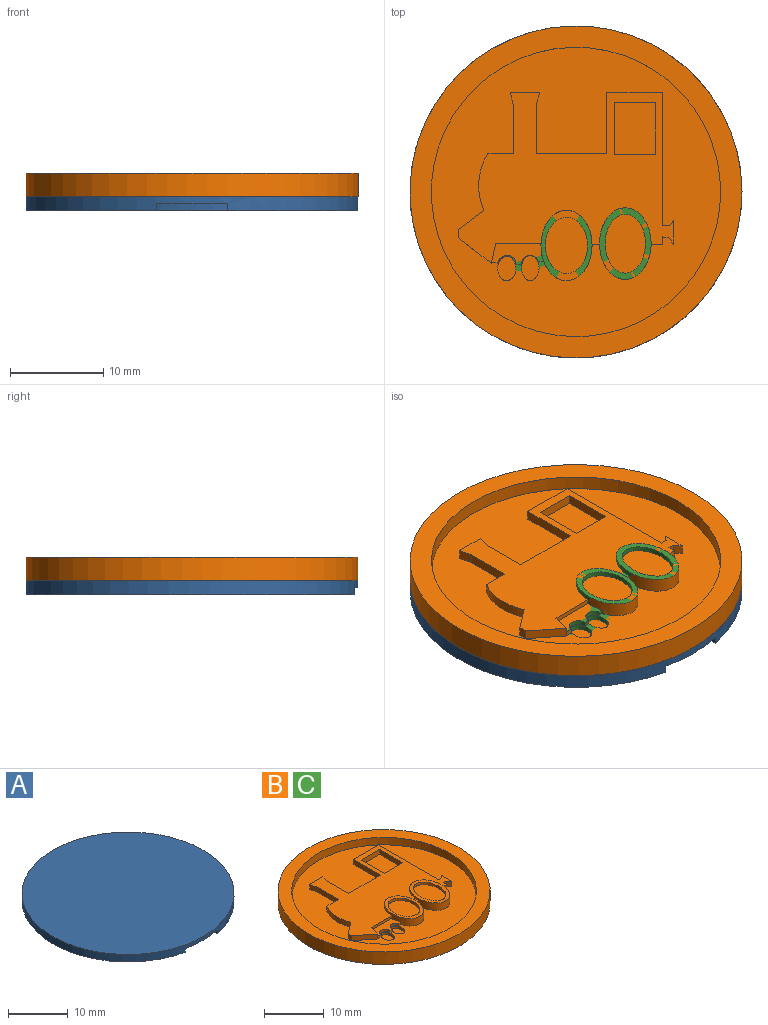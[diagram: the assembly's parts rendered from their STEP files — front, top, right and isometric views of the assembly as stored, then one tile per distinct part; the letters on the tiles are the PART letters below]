
ASSEMBLY  parts=3 mates=1
PART A: 170 faces, bbox 35.6x35.6x1.5 mm
  f0: plane 30.99x30.99mm, normal (0,0,-1), area 549.6mm2, adj f4,f5,f6,f7,f8,f9,f10,f11
  f1: plane 35.56x35.15mm, normal (0,0,-1), area 175mm2, adj f2,f165,f167,f169
  f2: cylinder r=17.78mm len=35.56mm, axis (0,0,-1), area 164.4mm2, adj f1,f3,f165,f167,f168
  f3: plane 35.56x35.56mm, normal (0,0,1), area 993.1mm2, adj f2
  f4: plane 1.49x0.76mm, normal (0,-1,0), area 1.1mm2, adj f0,f5,f15,f16
  f5: plane 7.05x0.76mm, normal (-1,0,0), area 5.4mm2, adj f0,f4,f6,f16
  f6: plane 1.49x0.76mm, normal (0,1,0), area 1.1mm2, adj f0,f5,f7,f16
  f7: plane 2.76x0.76mm, normal (1,0,0), area 2.1mm2, adj f0,f6,f8,f16
  f8: plane 2.79x0.76mm, normal (0,1,0), area 2.1mm2, adj f0,f7,f9,f16
  f9: plane 2.76x0.76mm, normal (-1,0,0), area 2.1mm2, adj f0,f8,f10,f16
  f10: plane 1.5x0.76mm, normal (0,1,0), area 1.1mm2, adj f0,f9,f11,f16
  f11: plane 7.05x0.76mm, normal (1,0,0), area 5.4mm2, adj f0,f10,f12,f16
  f12: plane 1.5x0.76mm, normal (0,-1,0), area 1.1mm2, adj f0,f11,f13,f16
  f13: plane 3.04x0.76mm, normal (-1,0,0), area 2.3mm2, adj f0,f12,f14,f16
  f14: plane 2.79x0.76mm, normal (0,-1,0), area 2.1mm2, adj f0,f13,f15,f16
  f15: plane 3.04x0.76mm, normal (1,0,0), area 2.3mm2, adj f0,f4,f14,f16
  f16: plane 7.05x5.78mm, normal (0,0,-1), area 24.5mm2, adj f4,f5,f6,f7,f8,f9,f10,f11
  f17: plane 7.05x0.76mm, normal (-1,0,0), area 5.4mm2, adj f0,f18,f41,f42
  f18: plane 2.19x0.76mm, normal (0,1,0), area 1.7mm2, adj f0,f17,f19,f42
  f19: extruded ~2.18x0.76mm, area 1.7mm2, adj f0,f18,f20,f42
  f20: extruded ~1.36x0.76mm, area 1.2mm2, adj f0,f19,f21,f42
  f21: extruded ~1.04x0.76mm, area 0.8mm2, adj f0,f20,f22,f42
  f22: extruded ~0.79x0.76mm, area 0.7mm2, adj f0,f21,f23,f42
  f23: plane 0.76x0.05mm, normal (1,0,0), area 0mm2, adj f0,f22,f24,f42
  f24: extruded ~0.97x0.76mm, area 0.9mm2, adj f0,f23,f25,f42
  f25: extruded ~1.09x0.76mm, area 0.9mm2, adj f0,f24,f26,f42
  f26: extruded ~1.51x0.76mm, area 1.3mm2, adj f0,f25,f27,f42
  f27: extruded ~1.89x0.76mm, area 1.5mm2, adj f0,f26,f41,f42
  f28: plane 0.93x0.76mm, normal (0,-1,0), area 0.7mm2, adj f29,f39,f42,f44
  f29: plane 1.84x0.76mm, normal (1,0,0), area 1.4mm2, adj f28,f30,f42,f44
  f30: plane 0.97x0.76mm, normal (0,1,0), area 0.7mm2, adj f29,f31,f42,f44
  f31: extruded ~0.91x0.76mm, area 0.7mm2, adj f30,f32,f42,f44
  f32: extruded ~0.76x0.72mm, area 0.6mm2, adj f31,f39,f42,f44
  f33: plane 1.57x0.76mm, normal (1,0,0), area 1.2mm2, adj f34,f40,f42,f43
  f34: plane 0.87x0.76mm, normal (0,1,0), area 0.7mm2, adj f33,f35,f42,f43
  f35: extruded ~0.88x0.76mm, area 0.7mm2, adj f34,f36,f42,f43
  f36: extruded ~0.76x0.62mm, area 0.5mm2, adj f35,f37,f42,f43
  f37: extruded ~0.76x0.58mm, area 0.5mm2, adj f36,f38,f42,f43
  f38: extruded ~0.94x0.76mm, area 0.7mm2, adj f37,f40,f42,f43
  f39: extruded ~1.25x0.88mm, area 1.3mm2, adj f28,f32,f42,f44
  f40: plane 0.79x0.76mm, normal (0,-1,0), area 0.6mm2, adj f33,f38,f42,f43
  f41: plane 2.64x0.76mm, normal (0,-1,0), area 2mm2, adj f0,f17,f27,f42
  f42: plane 7.05x5.23mm, normal (0,0,-1), area 27.1mm2, adj f17,f18,f19,f20,f21,f22,f23,f24
  f43: plane 2.02x1.57mm, normal (0,0,-1), area 2.9mm2, adj f33,f34,f35,f36,f37,f38,f40
  f44: plane 2.18x1.84mm, normal (0,0,-1), area 3.6mm2, adj f28,f29,f30,f31,f32,f39
  f45: extruded ~2.44x2.09mm, area 2.8mm2, adj f0,f46,f52,f53
  f46: extruded ~2.44x2.09mm, area 2.8mm2, adj f0,f45,f47,f53
  f47: extruded ~2.41x2.09mm, area 2.7mm2, adj f0,f46,f52,f53
  f48: extruded ~1.63x1.14mm, area 1.7mm2, adj f49,f51,f53,f54
  f49: extruded ~1.63x1.14mm, area 1.7mm2, adj f48,f50,f53,f54
  f50: extruded ~1.6x1.14mm, area 1.7mm2, adj f49,f51,f53,f54
  f51: extruded ~1.6x1.14mm, area 1.7mm2, adj f48,f50,f53,f54
  f52: extruded ~2.41x2.09mm, area 2.7mm2, adj f0,f45,f47,f53
  f53: plane 4.85x4.18mm, normal (0,0,-1), area 10.4mm2, adj f45,f46,f47,f48,f49,f50,f51,f52
  f54: plane 3.24x2.27mm, normal (0,0,-1), area 6mm2, adj f48,f49,f50,f51
  f55: extruded ~1.45x0.82mm, area 1.3mm2, adj f0,f56,f62,f63
  f56: extruded ~1.6x1.45mm, area 1.9mm2, adj f0,f55,f57,f63
  f57: plane 3.16x0.76mm, normal (-1,0,0), area 2.4mm2, adj f0,f56,f58,f63
  f58: plane 0.93x0.76mm, normal (0,1,0), area 0.7mm2, adj f0,f57,f59,f63
  f59: plane 3.09x0.76mm, normal (1,0,0), area 2.4mm2, adj f0,f58,f60,f63
  f60: extruded ~0.86x0.76mm, area 0.9mm2, adj f0,f59,f61,f63
  f61: extruded ~0.76x0.69mm, area 0.7mm2, adj f0,f60,f62,f63
  f62: plane 0.76x0.64mm, normal (0.59,0.81,0), area 0.6mm2, adj f0,f55,f61,f63
  f63: plane 4.76x2.9mm, normal (0,0,-1), area 5.6mm2, adj f55,f56,f57,f58,f59,f60,f61,f62
  f64: extruded ~2.19x1.82mm, area 2.5mm2, adj f0,f65,f73,f74
  f65: extruded ~2.19x1.81mm, area 2.5mm2, adj f0,f64,f66,f74
  f66: plane 2.57x0.76mm, normal (-1,0,0), area 2mm2, adj f0,f65,f67,f74
  f67: plane 0.9x0.76mm, normal (0,1,0), area 0.7mm2, adj f0,f66,f68,f74
  f68: plane 2.65x0.76mm, normal (1,0,0), area 2mm2, adj f0,f67,f69,f74
  f69: extruded ~1.3x0.91mm, area 1.4mm2, adj f0,f68,f70,f74
  f70: extruded ~1.3x0.88mm, area 1.4mm2, adj f0,f69,f71,f74
  f71: plane 2.65x0.76mm, normal (-1,0,0), area 2mm2, adj f0,f70,f72,f74
  f72: plane 0.93x0.76mm, normal (0,1,0), area 0.7mm2, adj f0,f71,f73,f74
  f73: plane 2.57x0.76mm, normal (1,0,0), area 2mm2, adj f0,f64,f72,f74
  f74: plane 4.76x3.62mm, normal (0,0,-1), area 9.2mm2, adj f64,f65,f66,f67,f68,f69,f70,f71
  f75: plane 4.67x0.76mm, normal (1,0,0), area 3.6mm2, adj f0,f76,f90,f91
  f76: plane 0.88x0.76mm, normal (0,-1,0), area 0.7mm2, adj f0,f75,f77,f91
  f77: plane 1.88x0.76mm, normal (-1,0,0), area 1.4mm2, adj f0,f76,f78,f91
  f78: extruded ~1.63x0.76mm, area 1.2mm2, adj f0,f77,f79,f91
  f79: plane 0.76x0.03mm, normal (0,-1,0), area 0mm2, adj f0,f78,f80,f91
  f80: plane 1x0.76mm, normal (0.9,-0.43,0), area 0.8mm2, adj f0,f79,f81,f91
  f81: plane 2.5x1.35mm, normal (0.88,-0.48,0), area 2.2mm2, adj f0,f80,f82,f91
  f82: plane 0.95x0.76mm, normal (0,-1,0), area 0.7mm2, adj f0,f81,f83,f91
  f83: plane 4.67x0.76mm, normal (-1,0,0), area 3.6mm2, adj f0,f82,f84,f91
  f84: plane 0.88x0.76mm, normal (0,1,0), area 0.7mm2, adj f0,f83,f85,f91
  f85: plane 1.86x0.76mm, normal (1,0,0), area 1.4mm2, adj f0,f84,f86,f91
  f86: extruded ~1.64x0.76mm, area 1.3mm2, adj f0,f85,f87,f91
  f87: plane 0.76x0.03mm, normal (0,1,0), area 0mm2, adj f0,f86,f88,f91
  f88: plane 1.01x0.76mm, normal (-0.91,0.42,0), area 0.8mm2, adj f0,f87,f89,f91
  f89: plane 2.49x1.36mm, normal (-0.88,0.48,0), area 2.2mm2, adj f0,f88,f90,f91
  f90: plane 0.95x0.76mm, normal (0,1,0), area 0.7mm2, adj f0,f75,f89,f91
  f91: plane 4.67x3.57mm, normal (0,0,-1), area 10.9mm2, adj f75,f76,f77,f78,f79,f80,f81,f82
  f92: plane 2.41x1.31mm, normal (0.88,0.48,0), area 2.1mm2, adj f0,f93,f109,f110
  f93: plane 0.99x0.76mm, normal (0,-1,0), area 0.8mm2, adj f0,f92,f94,f110
  f94: plane 1.04x0.76mm, normal (-0.9,-0.43,0), area 0.9mm2, adj f0,f93,f95,f110
  f95: extruded ~0.77x0.76mm, area 0.6mm2, adj f0,f94,f96,f110
  f96: plane 0.76x0.02mm, normal (0,-1,0), area 0mm2, adj f0,f95,f97,f110
  f97: extruded ~0.77x0.76mm, area 0.6mm2, adj f0,f96,f98,f110
  f98: plane 1.04x0.76mm, normal (0.89,-0.45,0), area 0.9mm2, adj f0,f97,f99,f110
  f99: plane 1.04x0.76mm, normal (0,-1,0), area 0.8mm2, adj f0,f98,f100,f110
  f100: plane 2.37x1.31mm, normal (-0.87,0.48,0), area 2.1mm2, adj f0,f99,f101,f110
  f101: plane 2.3x1.23mm, normal (-0.88,-0.47,0), area 2mm2, adj f0,f100,f102,f110
  f102: plane 0.98x0.76mm, normal (0,1,0), area 0.8mm2, adj f0,f101,f103,f110
  f103: plane 0.96x0.76mm, normal (0.91,0.42,0), area 0.8mm2, adj f0,f102,f104,f110
  f104: extruded ~0.76x0.74mm, area 0.6mm2, adj f0,f103,f105,f110
  f105: plane 0.76x0.03mm, normal (0,1,0), area 0mm2, adj f0,f104,f106,f110
  f106: extruded ~0.76x0.74mm, area 0.6mm2, adj f0,f105,f107,f110
  f107: plane 0.96x0.76mm, normal (-0.9,0.44,0), area 0.8mm2, adj f0,f106,f108,f110
  f108: plane 1.04x0.76mm, normal (0,1,0), area 0.8mm2, adj f0,f107,f109,f110
  f109: plane 2.26x1.23mm, normal (0.88,-0.48,0), area 2mm2, adj f0,f92,f108,f110
  f110: plane 4.67x3.78mm, normal (0,0,-1), area 8.4mm2, adj f92,f93,f94,f95,f96,f97,f98,f99
  f111: plane 4.67x0.76mm, normal (1,0,0), area 3.6mm2, adj f0,f112,f114,f115
  f112: plane 0.94x0.76mm, normal (0,-1,0), area 0.7mm2, adj f0,f111,f113,f115
  f113: plane 4.67x0.76mm, normal (-1,0,0), area 3.6mm2, adj f0,f112,f114,f115
  f114: plane 0.94x0.76mm, normal (0,1,0), area 0.7mm2, adj f0,f111,f113,f115
  f115: plane 4.67x0.94mm, normal (0,0,-1), area 4.4mm2, adj f111,f112,f113,f114
  f116: plane 4.67x0.76mm, normal (1,0,0), area 3.6mm2, adj f0,f117,f131,f132
  f117: plane 0.88x0.76mm, normal (0,-1,0), area 0.7mm2, adj f0,f116,f118,f132
  f118: plane 1.88x0.76mm, normal (-1,0,0), area 1.4mm2, adj f0,f117,f119,f132
  f119: extruded ~1.63x0.76mm, area 1.2mm2, adj f0,f118,f120,f132
  f120: plane 0.76x0.03mm, normal (0,-1,0), area 0mm2, adj f0,f119,f121,f132
  f121: plane 1x0.76mm, normal (0.9,-0.43,0), area 0.8mm2, adj f0,f120,f122,f132
  f122: plane 2.5x1.35mm, normal (0.88,-0.48,0), area 2.2mm2, adj f0,f121,f123,f132
  f123: plane 0.95x0.76mm, normal (0,-1,0), area 0.7mm2, adj f0,f122,f124,f132
  f124: plane 4.67x0.76mm, normal (-1,0,0), area 3.6mm2, adj f0,f123,f125,f132
  f125: plane 0.88x0.76mm, normal (0,1,0), area 0.7mm2, adj f0,f124,f126,f132
  f126: plane 1.86x0.76mm, normal (1,0,0), area 1.4mm2, adj f0,f125,f127,f132
  f127: extruded ~1.64x0.76mm, area 1.3mm2, adj f0,f126,f128,f132
  f128: plane 0.76x0.03mm, normal (0,1,0), area 0mm2, adj f0,f127,f129,f132
  f129: plane 1.01x0.76mm, normal (-0.91,0.42,0), area 0.8mm2, adj f0,f128,f130,f132
  f130: plane 2.49x1.36mm, normal (-0.88,0.48,0), area 2.2mm2, adj f0,f129,f131,f132
  f131: plane 0.95x0.76mm, normal (0,1,0), area 0.7mm2, adj f0,f116,f130,f132
  f132: plane 4.67x3.57mm, normal (0,0,-1), area 10.9mm2, adj f116,f117,f118,f119,f120,f121,f122,f123
  f133: extruded ~1.78x0.76mm, area 1.4mm2, adj f134,f146,f147,f163
  f134: extruded ~1.78x0.76mm, area 1.4mm2, adj f133,f135,f147,f163
  f135: extruded ~1.35x0.76mm, area 1.2mm2, adj f134,f136,f147,f163
  f136: extruded ~2.38x1.78mm, area 2.6mm2, adj f135,f137,f147,f163
  f137: extruded ~2.38x1.79mm, area 2.6mm2, adj f136,f146,f147,f163
  f138: extruded ~2.69x0.87mm, area 2.2mm2, adj f0,f139,f145,f147
  f139: extruded ~2.69x0.86mm, area 2.2mm2, adj f0,f138,f140,f147
  f140: extruded ~2.49x0.94mm, area 2.1mm2, adj f0,f139,f141,f147
  f141: extruded ~2.5x0.93mm, area 2.1mm2, adj f0,f140,f142,f147
  f142: extruded ~2.69x0.87mm, area 2.2mm2, adj f0,f141,f143,f147
  f143: extruded ~2.7x0.87mm, area 2.2mm2, adj f0,f142,f144,f147
  f144: extruded ~2.49x0.94mm, area 2.1mm2, adj f0,f143,f145,f147
  f145: extruded ~2.49x0.94mm, area 2.1mm2, adj f0,f138,f144,f147
  f146: extruded ~1.34x0.76mm, area 1.2mm2, adj f133,f137,f147,f163
  f147: plane 7.26x6.71mm, normal (0,0,-1), area 26mm2, adj f133,f134,f135,f136,f137,f138,f139,f140
  f148: extruded ~1.78x0.76mm, area 1.4mm2, adj f149,f161,f162,f164
  f149: extruded ~1.78x0.76mm, area 1.4mm2, adj f148,f150,f162,f164
  f150: extruded ~1.35x0.76mm, area 1.2mm2, adj f149,f151,f162,f164
  f151: extruded ~2.38x1.78mm, area 2.6mm2, adj f150,f152,f162,f164
  f152: extruded ~2.38x1.79mm, area 2.6mm2, adj f151,f161,f162,f164
  f153: extruded ~2.69x0.87mm, area 2.2mm2, adj f0,f154,f160,f162
  f154: extruded ~2.69x0.86mm, area 2.2mm2, adj f0,f153,f155,f162
  f155: extruded ~2.49x0.94mm, area 2.1mm2, adj f0,f154,f156,f162
  f156: extruded ~2.5x0.93mm, area 2.1mm2, adj f0,f155,f157,f162
  f157: extruded ~2.69x0.87mm, area 2.2mm2, adj f0,f156,f158,f162
  f158: extruded ~2.7x0.87mm, area 2.2mm2, adj f0,f157,f159,f162
  f159: extruded ~2.49x0.94mm, area 2.1mm2, adj f0,f158,f160,f162
  f160: extruded ~2.49x0.94mm, area 2.1mm2, adj f0,f153,f159,f162
  f161: extruded ~1.34x0.76mm, area 1.2mm2, adj f148,f152,f162,f164
  f162: plane 7.26x6.71mm, normal (0,0,-1), area 26mm2, adj f148,f149,f150,f151,f152,f153,f154,f155
  f163: plane 4.76x3.58mm, normal (0,0,-1), area 14.2mm2, adj f133,f134,f135,f136,f137,f146
  f164: plane 4.76x3.58mm, normal (0,0,-1), area 14.2mm2, adj f148,f149,f150,f151,f152,f161
  f165: plane 1.83x0.76mm, normal (1,0,0), area 1.4mm2, adj f1,f2,f168,f169
  f166: cylinder r=15.49mm len=30.99mm, axis (0,0,-1), area 74.2mm2, adj f0,f168
  f167: plane 1.83x0.76mm, normal (-1,0,0), area 1.4mm2, adj f1,f2,f168,f169
  f168: plane 33.78x32mm, normal (0,0,-1), area 63.9mm2, adj f2,f165,f166,f167,f169
  f169: cylinder r=16mm len=32mm, axis (0,0,-1), area 70.8mm2, adj f1,f165,f167,f168
PART B: 53 faces, bbox 35.6x35.6x2.6 mm
  f0: plane 2.11x1.02mm, normal (0.97,-0.24,0), area 1.1mm2, adj f1,f11,f12,f33,f45,f46
  f1: plane 30.99x30.99mm, normal (0,0,1), area 450.5mm2, adj f0,f5,f6,f7,f8,f9,f10,f11
  f2: cylinder r=17.78mm len=35.56mm, axis (0,0,-1), area 283.8mm2, adj f3,f4
  f3: plane 35.56x35.56mm, normal (0,0,1), area 239mm2, adj f2,f5
  f4: plane 35.56x35.56mm, normal (0,0,-1), area 993.1mm2, adj f2
  f5: cylinder r=15.49mm len=30.99mm, axis (0,0,1), area 148.4mm2, adj f1,f3
  f6: plane 5.02x1.02mm, normal (-1,0,0), area 5.1mm2, adj f1,f7,f32,f33
  f7: plane 2.76x1.02mm, normal (0,1,0), area 2.8mm2, adj f1,f6,f8,f33
  f8: cylinder r=6.6mm len=6.13mm, axis (0,0,-1), area 6.5mm2, adj f1,f7,f9,f33
  f9: plane 2.68x2.04mm, normal (-0.6,0.8,0), area 3.4mm2, adj f1,f8,f10,f33
  f10: plane 1.02x0.88mm, normal (-1,0,0), area 0.9mm2, adj f1,f9,f11,f33
  f11: plane 3.45x2.73mm, normal (-0.62,-0.78,0), area 4.5mm2, adj f0,f1,f10,f33
  f12: plane 4.83x0.51mm, normal (0,-1,0), area 2.5mm2, adj f0,f33,f37,f46
  f13: plane 1.02x0.81mm, normal (0,-1,0), area 0.8mm2, adj f1,f33,f37,f40
  f14: plane 1.21x1.02mm, normal (0,-1,0), area 1.2mm2, adj f1,f15,f33,f40
  f15: plane 1.02x0.84mm, normal (1,0,0), area 0.9mm2, adj f1,f14,f16,f33
  f16: plane 1.02x0.63mm, normal (-0.14,-0.99,0), area 0.7mm2, adj f1,f15,f17,f33
  f17: plane 1.02x0.7mm, normal (-0.77,-0.64,0), area 0.9mm2, adj f1,f16,f18,f33
  f18: plane 2.55x1.02mm, normal (1,0,0), area 2.6mm2, adj f1,f17,f19,f33
  f19: plane 1.02x0.6mm, normal (-0.79,0.61,0), area 0.8mm2, adj f1,f18,f20,f33
  f20: plane 1.02x0.76mm, normal (0,1,0), area 0.8mm2, adj f1,f19,f21,f33
  f21: plane 14.25x1.02mm, normal (1,0,0), area 14.5mm2, adj f1,f20,f22,f33
  f22: plane 5.94x1.02mm, normal (0,1,0), area 6mm2, adj f1,f21,f23,f33
  f23: plane 6.45x1.02mm, normal (-1,0,0), area 6.6mm2, adj f1,f22,f24,f33
  f24: plane 7.55x1.02mm, normal (0,1,0), area 7.7mm2, adj f1,f23,f25,f33
  f25: plane 5.23x1.02mm, normal (1,0,0), area 5.3mm2, adj f1,f24,f26,f33
  f26: plane 1.26x1.02mm, normal (0.96,-0.29,0), area 1.3mm2, adj f1,f25,f27,f33
  f27: plane 3.14x1.02mm, normal (0,1,0), area 3.2mm2, adj f1,f26,f32,f33
  f28: plane 5.5x1.02mm, normal (-1,0,0), area 5.6mm2, adj f29,f31,f33,f34
  f29: plane 4.41x1.02mm, normal (0,1,0), area 4.5mm2, adj f28,f30,f33,f34
  f30: plane 5.5x1.02mm, normal (1,0,0), area 5.6mm2, adj f29,f31,f33,f34
  f31: plane 4.41x1.02mm, normal (0,-1,0), area 4.5mm2, adj f28,f30,f33,f34
  f32: plane 1.49x1.02mm, normal (-0.97,-0.22,0), area 1.6mm2, adj f1,f6,f27,f33
  f33: plane 23.03x18.3mm, normal (0,0,1), area 197.4mm2, adj f0,f6,f7,f8,f9,f10,f11,f12
  f34: plane 5.5x4.41mm, normal (0,0,1), area 24.3mm2, adj f28,f29,f30,f31
  f35: plane 7.54x5.47mm, normal (0,0,1), area 11.1mm2, adj f36,f37
  f36: extruded ~6.01x4.52mm, area 8.4mm2, adj f35,f51
  f37: extruded ~7.54x5.47mm, area 20.3mm2, adj f1,f12,f13,f33,f35,f44,f46
  f38: plane 7.68x5.52mm, normal (0,0,1), area 11.9mm2, adj f39,f40
  f39: extruded ~6.31x4.31mm, area 8.6mm2, adj f38,f52
  f40: extruded ~7.68x5.52mm, area 21mm2, adj f1,f13,f14,f33,f38
  f41: cylinder r=0.95mm len=1.89mm, axis (0,0,-1), area 1.5mm2, adj f1,f42,f45,f46
  f42: plane 0.62x0.51mm, normal (0.08,-1,0), area 0.3mm2, adj f1,f41,f43,f46
  f43: cylinder r=0.92mm len=1.82mm, axis (0,0,-1), area 1.4mm2, adj f1,f42,f44,f46
  f44: plane 0.55x0.52mm, normal (0.28,-0.96,0), area 0.3mm2, adj f1,f37,f43,f46
  f45: plane 0.75x0.51mm, normal (-0.07,-1,0), area 0.4mm2, adj f0,f1,f41,f46
  f46: plane 5.63x2.31mm, normal (0,0,1), area 8.4mm2, adj f0,f12,f37,f41,f42,f43,f44,f45
  f47: extruded ~2.68x1.87mm, area 3.7mm2, adj f1,f48
  f48: plane 2.68x1.87mm, normal (0,0,1), area 3.9mm2, adj f47
  f49: extruded ~2.61x1.95mm, area 3.7mm2, adj f1,f50
  f50: plane 2.61x1.95mm, normal (0,0,1), area 4mm2, adj f49
  f51: plane 6.01x4.52mm, normal (0,0,1), area 21.3mm2, adj f36
  f52: plane 6.31x4.31mm, normal (0,0,1), area 21.4mm2, adj f39
PART C: same geometry as B
PLACE A t=(-6.45,-25.08,-33.67)mm
PLACE B t=(-6.45,-25.08,-32.14)mm fixed
PLACE C t=(-6.45,-25.08,-32.14)mm
MATE fastened A.f2 <-> B.f2  axis (0,0,1) through (-6.45,-25.08,-32.14)mm
